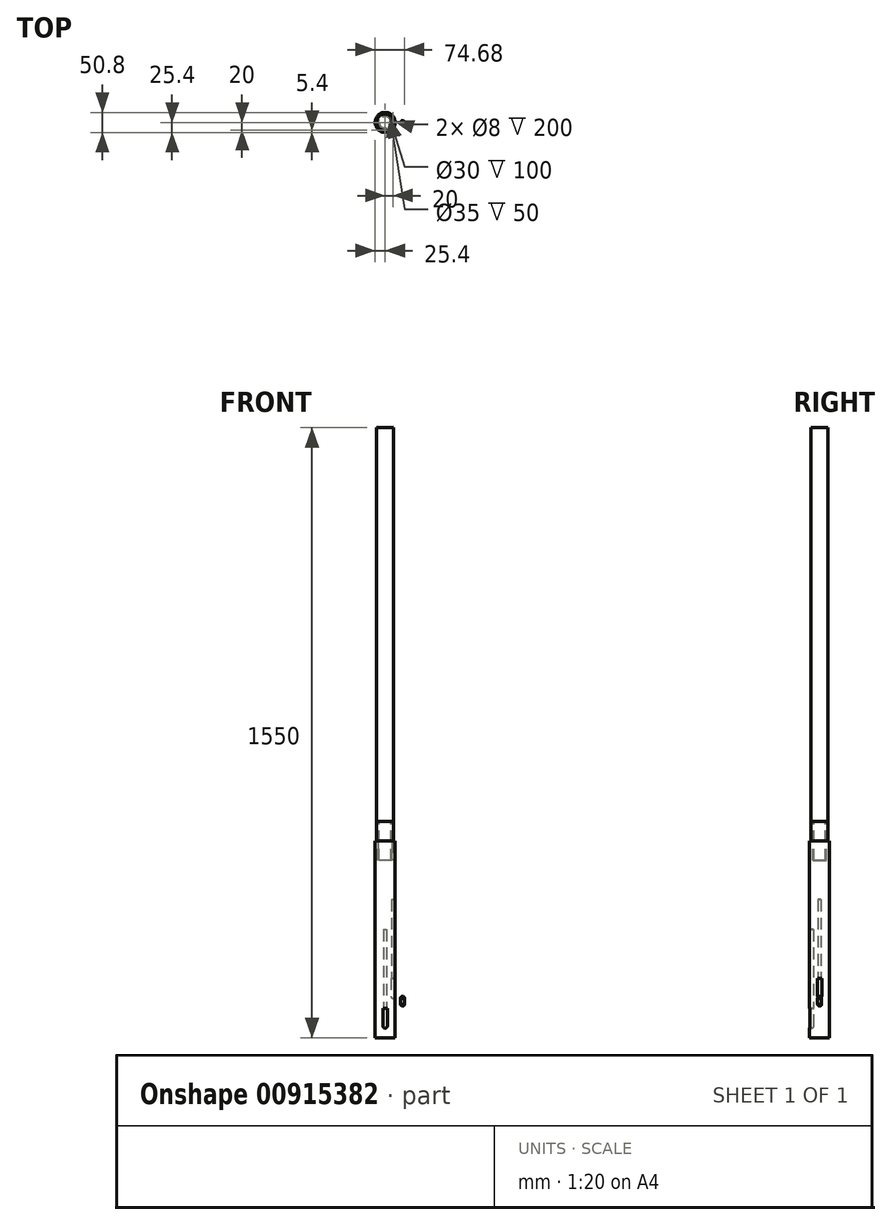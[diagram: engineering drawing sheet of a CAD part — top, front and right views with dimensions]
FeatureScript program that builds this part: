
annotation { "Feature Type Name" : "Feature", "Feature Type Description" : "" }
export const myFeature = defineFeature(function(context is Context, id is Id, definition is map)
    precondition{}
    {
        {
            var Q0;
            Q0=qCreatedBy(makeId("Front.planeOp"),FACE);
            var sketch = newSketch(context, id + "F0", { "sketchPlane" : qUnion([Q0])});
            skLineSegment(sketch, "E0", {"start": v(15, 0) * mm, "end": v(17.5, 0) * mm});
            skLineSegment(sketch, "E1", {"start": v(17.5, 0) * mm, "end": v(17.5, 50) * mm});
            skLineSegment(sketch, "E2", {"start": v(17.5, 50) * mm, "end": v(21.5, 50) * mm});
            skLineSegment(sketch, "E3", {"start": v(21.5, 50) * mm, "end": v(21.5, 100) * mm});
            skLineSegment(sketch, "E4", {"start": v(21.5, 100) * mm, "end": v(15, 100) * mm});
            skLineSegment(sketch, "E5", {"start": v(15, 100) * mm, "end": v(15, 0) * mm});
            skLineSegment(sketch, "E6", {"start": v(21.5, 100) * mm, "end": v(21.5, 1100) * mm});
            skLineSegment(sketch, "E7", {"start": v(21.5, 1100) * mm, "end": v(0, 1100) * mm});
            skLineSegment(sketch, "E8", {"start": v(0, 1100) * mm, "end": v(0, 0) * mm});
            skLineSegment(sketch, "E9", {"start": v(0, 0) * mm, "end": v(15, 0) * mm});
            skLineSegment(sketch, "E10", {"start": v(0, 0) * mm, "end": v(0, -65.65) * mm, "construction": true});
            skLineSegment(sketch, "E11", {"start": v(21.5, 50) * mm, "end": v(25.4, 50) * mm});
            skLineSegment(sketch, "E12", {"start": v(25.4, 50) * mm, "end": v(25.4, -450) * mm});
            skLineSegment(sketch, "E13", {"start": v(25.4, -450) * mm, "end": v(0, -450) * mm});
            skLineSegment(sketch, "E14", {"start": v(0, -450) * mm, "end": v(0, 0) * mm});
            skSolve(sketch);
        }
        {
            var Q0;
            Q0=makeQuery(id+"F0.imprint","IMPRINT",FACE,{"disambiguationData":[TD([[makeQuery(id+"F0.imprint","IMPRINT",EDGE,{"derivedFrom":sQuery(id+"F0.wireOp",EDGE,"E4")}),-1.0]])]});
            var Q1;
            Q1=sQuery(id+"F0.wireOp",EDGE,"E8");
            revolve(context, id + "F1", {"surfaceOperationType" : NewSurfaceOperationType.NEW, "entities" : qUnion([Q0]), "axis" : qUnion([Q1]), "revolveType" : RevolveType.FULL});
        }
        {
            var Q0;
            Q0=makeQuery(id+"F0.imprint","IMPRINT",FACE,{"disambiguationData":[TD([[makeQuery(id+"F0.imprint","IMPRINT",EDGE,{"derivedFrom":sQuery(id+"F0.wireOp",EDGE,"E0")}),1.0]])]});
            var Q1;
            Q1=sQuery(id+"F0.wireOp",EDGE,"E8");
            revolve(context, id + "F2", {"surfaceOperationType" : NewSurfaceOperationType.NEW, "entities" : qUnion([Q0]), "axis" : qUnion([Q1]), "revolveType" : RevolveType.FULL});
        }
        {
            var Q0;
            Q0=makeQuery(id+"F0.imprint","IMPRINT",FACE,{"disambiguationData":[TD([[makeQuery(id+"F0.imprint","IMPRINT",EDGE,{"derivedFrom":sQuery(id+"F0.wireOp",EDGE,"E0")}),-1.0]])]});
            var Q1;
            Q1=sQuery(id+"F0.wireOp",EDGE,"E14");
            revolve(context, id + "F3", {"surfaceOperationType" : NewSurfaceOperationType.NEW, "entities" : qUnion([Q0]), "axis" : qUnion([Q1]), "revolveType" : RevolveType.FULL});
        }
        {
            var Q0;
            Q0=qCreatedBy(makeId("Front.planeOp"),FACE);
            var sketch = newSketch(context, id + "F4", { "sketchPlane" : qUnion([Q0])});
            skLineSegment(sketch, "E15", {"start": v(20, -299.2) * mm, "end": v(20, -350) * mm});
            skLineSegment(sketch, "E16", {"start": v(20, -350) * mm, "end": v(25.5, -350) * mm});
            skLineSegment(sketch, "E17", {"start": v(25.5, -350) * mm, "end": v(25.5, -299.2) * mm});
            skLineSegment(sketch, "E18", {"start": v(25.5, -299.2) * mm, "end": v(20, -299.2) * mm});
            skLineSegment(sketch, "E19", {"start": v(0, 0) * mm, "end": v(0, -392.46) * mm, "construction": true});
            skSolve(sketch);
        }
        {
            var Q0;
            Q0=qSketchRegion(id+"F4",true);
            var Q1;
            Q1=sQuery(id+"F4.wireOp",EDGE,"E15");
            revolve(context, id + "F5", {"operationType" : NewBodyOperationType.REMOVE, "surfaceOperationType" : NewSurfaceOperationType.NEW, "entities" : qUnion([Q0]), "axis" : qUnion([Q1]), "revolveType" : RevolveType.FULL, "oppositeDirection" : true});
        }
        {
            var Q0;
            Q0=qSketchRegion(id+"F4",true);
            extrude(context, id + "F6", {"entities" : qUnion([Q0]), "operationType" : NewBodyOperationType.REMOVE, "oppositeDirection" : true, "depth" : 5.5 * mm, "offsetDistance" : 25 * mm, "hasSecondDirection" : true, "secondDirectionOppositeDirection" : false, "secondDirectionDepth" : 5.5 * mm});
        }
        {
            var Q0;
            Q0=makeQuery(id+"F5.boolean.opBoolean","COPY",EDGE,{"derivedFrom":makeQuery(id+"F5.opRevolve","SWEPT_EDGE",EDGE,{"disambiguationData":[OSD([sQuery(id+"F4.wireOp",EDGE,"E16"),sQuery(id+"F4.wireOp",EDGE,"E17")])]})});
            fillet(context, id + "F7", {"entities" : qUnion([Q0]), "radius" : 5.5 * mm, "tangentPropagation" : true, "allowEdgeOverflow" : false});
        }
        {
            var Q0;
            {var subQ0=sQuery(id+"F4.wireOp",EDGE,"E18");Q0=makeQuery(id+"F6.boolean.opBoolean","MERGE",FACE,{"derivedFrom":[makeQuery(id+"F5.boolean.opBoolean","COPY",FACE,{"derivedFrom":makeQuery(id+"F5.opRevolve","SWEPT_FACE",FACE,{"disambiguationData":[OSD([subQ0])]})})],"fromTools":[makeQuery(id+"F6.opExtrude","SWEPT_FACE",FACE,{"disambiguationData":[OSD([subQ0])]})]});}
            var sketch = newSketch(context, id + "F8", { "sketchPlane" : qUnion([Q0])});
            skCircle(sketch, "E20", {"center": v(20, 0) * mm, "radius": 4 * mm});
            skSolve(sketch);
        }
        {
            var Q0;
            Q0=makeQuery(id+"F8.imprint","IMPRINT",FACE,{"disambiguationData":[TD([[makeQuery(id+"F8.imprint","IMPRINT",EDGE,{"derivedFrom":sQuery(id+"F8.wireOp",EDGE,"E20")}),1.0]])]});
            extrude(context, id + "F9", {"entities" : qUnion([Q0]), "operationType" : NewBodyOperationType.REMOVE, "oppositeDirection" : true, "depth" : 200 * mm, "offsetDistance" : 25 * mm});
        }
        {
            var Q0;
            Q0=qCreatedBy(makeId("Right.planeOp"),FACE);
            var sketch = newSketch(context, id + "F10", { "sketchPlane" : qUnion([Q0])});
            skLineSegment(sketch, "E21", {"start": v(-25.5, -375) * mm, "end": v(-25.5, -425.8) * mm});
            skLineSegment(sketch, "E22", {"start": v(-25.5, -425.8) * mm, "end": v(-20, -425.8) * mm});
            skLineSegment(sketch, "E23", {"start": v(-20, -425.8) * mm, "end": v(-20, -375) * mm});
            skLineSegment(sketch, "E24", {"start": v(-20, -375) * mm, "end": v(-25.5, -375) * mm});
            skLineSegment(sketch, "E25", {"start": v(0, -450.32) * mm, "end": v(0, -383.23) * mm, "construction": true});
            skSolve(sketch);
        }
        {
            var Q0;
            Q0=qSketchRegion(id+"F10",true);
            var Q1;
            Q1=sQuery(id+"F10.wireOp",EDGE,"E23");
            revolve(context, id + "F11", {"operationType" : NewBodyOperationType.REMOVE, "surfaceOperationType" : NewSurfaceOperationType.NEW, "entities" : qUnion([Q0]), "axis" : qUnion([Q1]), "revolveType" : RevolveType.FULL, "oppositeDirection" : true});
        }
        {
            var Q0;
            Q0=qSketchRegion(id+"F10",true);
            extrude(context, id + "F12", {"entities" : qUnion([Q0]), "operationType" : NewBodyOperationType.REMOVE, "oppositeDirection" : true, "depth" : 5.5 * mm, "offsetDistance" : 25 * mm, "hasSecondDirection" : true, "secondDirectionOppositeDirection" : false, "secondDirectionDepth" : 5.5 * mm});
        }
        {
            var Q0;
            Q0=makeQuery(id+"F11.boolean.opBoolean","COPY",EDGE,{"derivedFrom":makeQuery(id+"F11.opRevolve","SWEPT_EDGE",EDGE,{"disambiguationData":[OSD([sQuery(id+"F10.wireOp",EDGE,"E21"),sQuery(id+"F10.wireOp",EDGE,"E22")])]})});
            fillet(context, id + "F13", {"entities" : qUnion([Q0]), "radius" : 5.5 * mm, "tangentPropagation" : true, "allowEdgeOverflow" : false});
        }
        {
            var Q0;
            {var subQ0=sQuery(id+"F10.wireOp",EDGE,"E24");Q0=makeQuery(id+"F12.boolean.opBoolean","MERGE",FACE,{"derivedFrom":[makeQuery(id+"F11.boolean.opBoolean","COPY",FACE,{"derivedFrom":makeQuery(id+"F11.opRevolve","SWEPT_FACE",FACE,{"disambiguationData":[OSD([subQ0])]})})],"fromTools":[makeQuery(id+"F12.opExtrude","SWEPT_FACE",FACE,{"disambiguationData":[OSD([subQ0])]})]});}
            var sketch = newSketch(context, id + "F14", { "sketchPlane" : qUnion([Q0])});
            skCircle(sketch, "E26", {"center": v(0, 20) * mm, "radius": 4 * mm});
            skSolve(sketch);
        }
        {
            var Q0;
            Q0=qSketchRegion(id+"F14",true);
            extrude(context, id + "F15", {"entities" : qUnion([Q0]), "operationType" : NewBodyOperationType.REMOVE, "oppositeDirection" : true, "depth" : 200 * mm, "offsetDistance" : 25 * mm});
        }
        {
            var Q0;
            Q0=qCreatedBy(makeId("Front.planeOp"),FACE);
            var sketch = newSketch(context, id + "F16", { "sketchPlane" : qUnion([Q0])});
            skLineSegment(sketch, "E27.bottom", {"start": v(44.28, -349.8) * mm, "end": v(49.28, -349.8) * mm});
            skLineSegment(sketch, "E27.top", {"start": v(44.28, -364.8) * mm, "end": v(49.28, -364.8) * mm});
            skLineSegment(sketch, "E27.left", {"start": v(44.28, -349.8) * mm, "end": v(44.28, -364.8) * mm});
            skLineSegment(sketch, "E27.right", {"start": v(49.28, -350.3) * mm, "end": v(49.28, -364.8) * mm});
            skArc(sketch, "E28", {"start": v(49.28, -364.8) * mm, "mid": v(47.81, -368.33) * mm, "end": v(44.28, -369.8) * mm});
            skArc(sketch, "E29", {"start": v(49.28, -349.8) * mm, "mid": v(47.81, -346.26) * mm, "end": v(44.28, -344.8) * mm});
            skLineSegment(sketch, "E30", {"start": v(44.28, -344.8) * mm, "end": v(44.28, -349.8) * mm});
            skLineSegment(sketch, "E31", {"start": v(44.28, -369.8) * mm, "end": v(44.28, -364.8) * mm});
            skLineSegment(sketch, "E32", {"start": v(49.28, -350.3) * mm, "end": v(48.78, -350.3) * mm});
            skLineSegment(sketch, "E33", {"start": v(48.78, -350.3) * mm, "end": v(48.78, -349.8) * mm});
            skSolve(sketch);
        }
        {
            var Q0;
            Q0=makeQuery(id+"F16.imprint","IMPRINT",FACE,{"disambiguationData":[TD([[makeQuery(id+"F16.imprint","IMPRINT",EDGE,{"derivedFrom":sQuery(id+"F16.wireOp",EDGE,"E27.bottom")}),-1.0]])]});
            var Q1;
            Q1=makeQuery(id+"F16.imprint","IMPRINT",FACE,{"disambiguationData":[TD([[makeQuery(id+"F16.imprint","IMPRINT",EDGE,{"derivedFrom":sQuery(id+"F16.wireOp",EDGE,"E27.bottom")}),1.0]])]});
            var Q2;
            Q2=sQuery(id+"F16.wireOp",EDGE,"E27.left");
            revolve(context, id + "F17", {"surfaceOperationType" : NewSurfaceOperationType.NEW, "entities" : qUnion([Q0, Q1]), "axis" : qUnion([Q2]), "revolveType" : RevolveType.FULL});
        }
        {
            var Q0;
            Q0=makeQuery(id+"F17.opRevolve","SWEPT_FACE",FACE,{"disambiguationData":[OSD([sQuery(id+"F16.wireOp",EDGE,"E27.top")])]});
            var sketch = newSketch(context, id + "F18", { "sketchPlane" : qUnion([Q0])});
            skLineSegment(sketch, "E34.bottom", {"start": v(45.78, -1.5) * mm, "end": v(42.78, -1.5) * mm});
            skLineSegment(sketch, "E34.top", {"start": v(45.78, 1.5) * mm, "end": v(42.78, 1.5) * mm});
            skLineSegment(sketch, "E34.left", {"start": v(45.78, -1.5) * mm, "end": v(45.78, 1.5) * mm});
            skLineSegment(sketch, "E34.right", {"start": v(42.78, -1.5) * mm, "end": v(42.78, 1.5) * mm});
            skPoint(sketch, "E34.middle", {"position": v(44.28, 0) * mm});
            skLineSegment(sketch, "E35.bottom", {"start": v(43.53, -4) * mm, "end": v(45.03, -4) * mm});
            skLineSegment(sketch, "E35.top", {"start": v(43.53, -2.5) * mm, "end": v(45.03, -2.5) * mm});
            skLineSegment(sketch, "E35.left", {"start": v(43.53, -4) * mm, "end": v(43.53, -2.5) * mm});
            skLineSegment(sketch, "E35.right", {"start": v(45.03, -4) * mm, "end": v(45.03, -2.5) * mm});
            skPoint(sketch, "E35.middle", {"position": v(44.28, -3.25) * mm});
            skLineSegment(sketch, "E36", {"start": v(44.28, 0) * mm, "end": v(44.28, -3.25) * mm, "construction": true});
            skLineSegment(sketch, "E37.1.0", {"start": v(48.12, -1.35) * mm, "end": v(46.82, -0.6) * mm});
            skLineSegment(sketch, "E37.1.1", {"start": v(47.37, -2.65) * mm, "end": v(48.12, -1.35) * mm});
            skLineSegment(sketch, "E37.1.2", {"start": v(47.37, -2.65) * mm, "end": v(46.07, -1.9) * mm});
            skLineSegment(sketch, "E37.1.3", {"start": v(46.07, -1.9) * mm, "end": v(46.82, -0.6) * mm});
            skLineSegment(sketch, "E37.2.0", {"start": v(47.37, 2.65) * mm, "end": v(46.07, 1.9) * mm});
            skLineSegment(sketch, "E37.2.1", {"start": v(48.12, 1.35) * mm, "end": v(47.37, 2.65) * mm});
            skLineSegment(sketch, "E37.2.2", {"start": v(48.12, 1.35) * mm, "end": v(46.82, 0.6) * mm});
            skLineSegment(sketch, "E37.2.3", {"start": v(46.82, 0.6) * mm, "end": v(46.07, 1.9) * mm});
            skLineSegment(sketch, "E37.3.0", {"start": v(43.53, 4) * mm, "end": v(43.53, 2.5) * mm});
            skLineSegment(sketch, "E37.3.1", {"start": v(45.03, 4) * mm, "end": v(43.53, 4) * mm});
            skLineSegment(sketch, "E37.3.2", {"start": v(45.03, 4) * mm, "end": v(45.03, 2.5) * mm});
            skLineSegment(sketch, "E37.3.3", {"start": v(45.03, 2.5) * mm, "end": v(43.53, 2.5) * mm});
            skLineSegment(sketch, "E37.4.0", {"start": v(40.44, 1.35) * mm, "end": v(41.74, 0.6) * mm});
            skLineSegment(sketch, "E37.4.1", {"start": v(41.19, 2.65) * mm, "end": v(40.44, 1.35) * mm});
            skLineSegment(sketch, "E37.4.2", {"start": v(41.19, 2.65) * mm, "end": v(42.49, 1.9) * mm});
            skLineSegment(sketch, "E37.4.3", {"start": v(42.49, 1.9) * mm, "end": v(41.74, 0.6) * mm});
            skLineSegment(sketch, "E37.5.0", {"start": v(41.19, -2.65) * mm, "end": v(42.49, -1.9) * mm});
            skLineSegment(sketch, "E37.5.1", {"start": v(40.44, -1.35) * mm, "end": v(41.19, -2.65) * mm});
            skLineSegment(sketch, "E37.5.2", {"start": v(40.44, -1.35) * mm, "end": v(41.74, -0.6) * mm});
            skLineSegment(sketch, "E37.5.3", {"start": v(41.74, -0.6) * mm, "end": v(42.49, -1.9) * mm});
            skSolve(sketch);
        }
        {
            var Q0;
            Q0 = qSketchRegion(id + "F18", true);
            extrude(context, id + "F19", {"entities" : qUnion([Q0]), "operationType" : NewBodyOperationType.ADD, "depth" : 0.5 * mm, "offsetDistance" : 25 * mm});
        }
        {
            var Q0;
            Q0=makeQuery(id+"F16.imprint","IMPRINT",FACE,{"disambiguationData":[TD([[makeQuery(id+"F16.imprint","IMPRINT",EDGE,{"derivedFrom":sQuery(id+"F16.wireOp",EDGE,"E27.top")}),-1.0]])]});
            var Q1;
            Q1=sQuery(id+"F16.wireOp",EDGE,"E31");
            revolve(context, id + "F20", {"surfaceOperationType" : NewSurfaceOperationType.NEW, "entities" : qUnion([Q0]), "axis" : qUnion([Q1]), "revolveType" : RevolveType.FULL});
        }
    });
